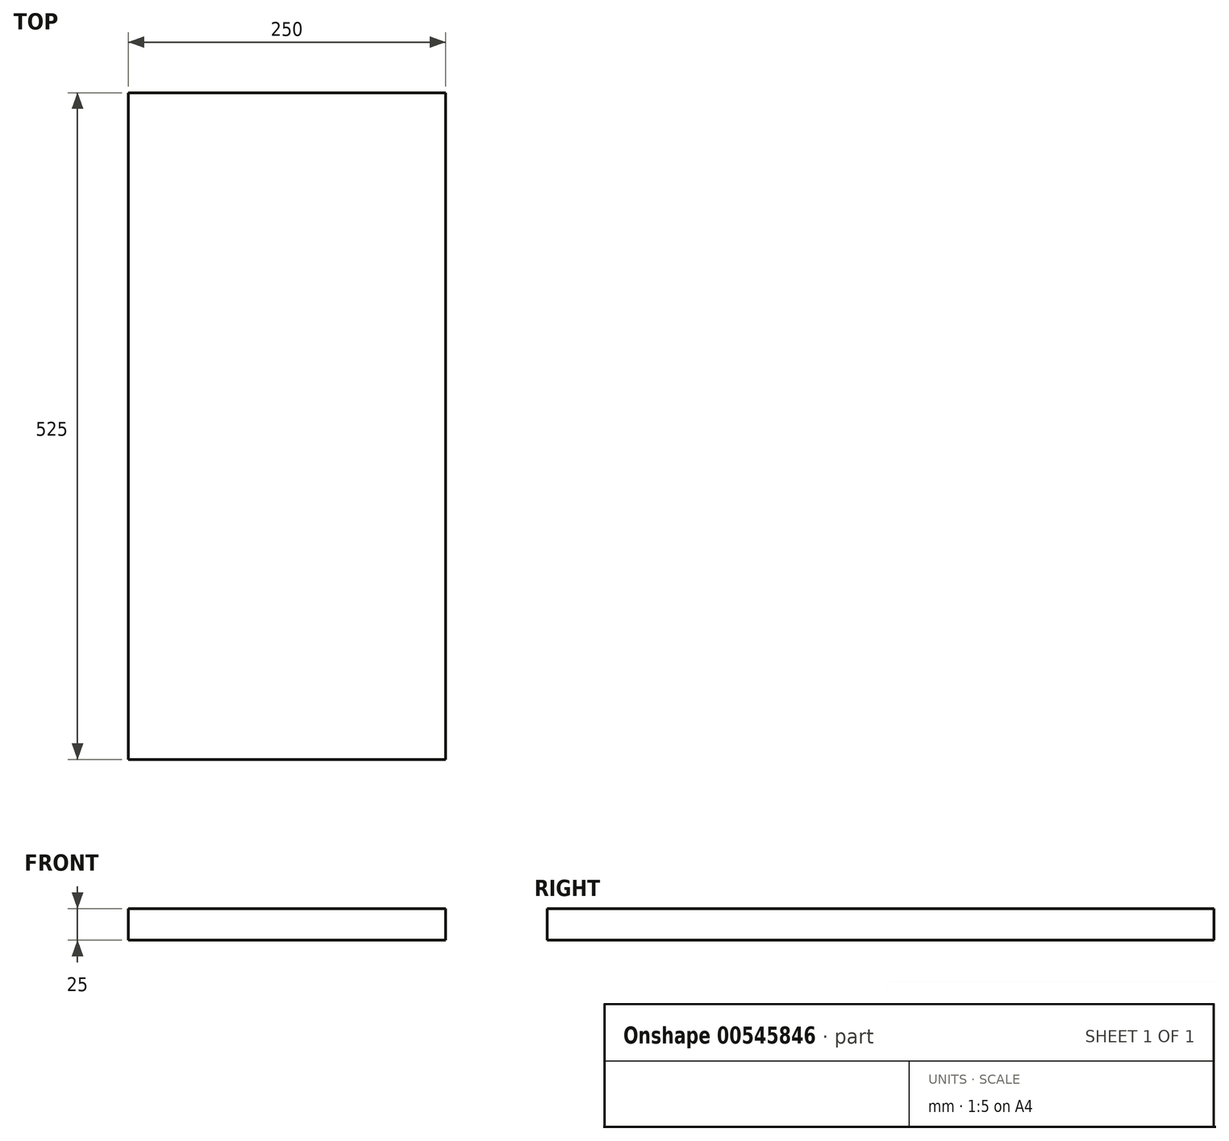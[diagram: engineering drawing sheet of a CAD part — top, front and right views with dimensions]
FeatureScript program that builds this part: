
annotation { "Feature Type Name" : "Feature", "Feature Type Description" : "" }
export const myFeature = defineFeature(function(context is Context, id is Id, definition is map)
    precondition{}
    {
        {
            var Q0;
            Q0=qCreatedBy(makeId("Top.planeOp"),FACE);
            var sketch = newSketch(context, id + "F0", { "sketchPlane" : qUnion([Q0])});
            skLineSegment(sketch, "E0", {"start": v(0, 1000) * mm, "end": v(0, -700) * mm, "construction": true});
            skLineSegment(sketch, "E1", {"start": v(-675, 1000) * mm, "end": v(0, 1000) * mm, "construction": true});
            skLineSegment(sketch, "E2", {"start": v(-675, -350) * mm, "end": v(-675, -700) * mm, "construction": true});
            skLineSegment(sketch, "E3", {"start": v(-675, -700) * mm, "end": v(-425, -700) * mm, "construction": true});
            skLineSegment(sketch, "E4.MirrorCS", {"start": v(675, 1000) * mm, "end": v(0, 1000) * mm, "construction": true});
            skLineSegment(sketch, "E5.MirrorCS", {"start": v(0, -700) * mm, "end": v(425, -700) * mm, "construction": true});
            skLineSegment(sketch, "E6", {"start": v(-425, -700) * mm, "end": v(-675, -350) * mm, "construction": true});
            skLineSegment(sketch, "E7", {"start": v(675, 1000) * mm, "end": v(675, -350) * mm, "construction": true});
            skLineSegment(sketch, "E8", {"start": v(425, -700) * mm, "end": v(-425, -700) * mm, "construction": true});
            skLineSegment(sketch, "E9", {"start": v(675, -350) * mm, "end": v(425, -700) * mm, "construction": true});
            skLineSegment(sketch, "E10", {"start": v(-675, -350) * mm, "end": v(-675, 1000) * mm, "construction": true});
            skLineSegment(sketch, "E11", {"start": v(-425, 350) * mm, "end": v(0, 350) * mm, "construction": true});
            skLineSegment(sketch, "E12.MirrorCS", {"start": v(425, 350) * mm, "end": v(0, 350) * mm, "construction": true});
            skLineSegment(sketch, "E13", {"start": v(-425, 350) * mm, "end": v(-425, -700) * mm, "construction": true});
            skLineSegment(sketch, "E14", {"start": v(425, 350) * mm, "end": v(425, -700) * mm, "construction": true});
            skLineSegment(sketch, "E15.bottom", {"start": v(-425, 350) * mm, "end": v(-675, 350) * mm});
            skLineSegment(sketch, "E15.top", {"start": v(-425, -175) * mm, "end": v(-675, -175) * mm});
            skLineSegment(sketch, "E15.left", {"start": v(-425, 350) * mm, "end": v(-425, -175) * mm});
            skLineSegment(sketch, "E15.right", {"start": v(-675, 350) * mm, "end": v(-675, -175) * mm});
            skLineSegment(sketch, "E16.MirrorCS", {"start": v(-675, -700) * mm, "end": v(-675, -175) * mm});
            skLineSegment(sketch, "E17.MirrorCS", {"start": v(-425, -700) * mm, "end": v(-425, -175) * mm});
            skSolve(sketch);
        }
        {
            var Q0;
            Q0=makeQuery(id+"F0.imprint","IMPRINT",FACE,{"disambiguationData":[TD([[makeQuery(id+"F0.imprint","IMPRINT",EDGE,{"derivedFrom":sQuery(id+"F0.wireOp",EDGE,"E15.bottom")}),1.0]])]});
            extrude(context, id + "F1", {"entities" : qUnion([Q0]), "depth" : 25 * mm, "offsetDistance" : 25 * mm});
        }
    });
